# Revit family: Showerhead_Contemporary_Kiwami-Renesse_TS170A_TOTO
name_source: partatom
category: Plumbing Fixtures
revit_build: Autodesk Revit Architecture 2013 (Build: 20130531_2115(x64)
units: mm (PartAtom-declared; Revit-internal decimal feet)

## types (1)
- TS170A
    04 CSI = 22 41 39
    95 CSI = 15416
    Assembly Code = D2010710
    CAD Drawing URL = http://assets.totousa.com
    CW Connection = Yes
    CWFU = 0
    Cold Water Connection Diameter = 1"
    Cold Water Connection Radius = 1/2"
    Cold Water Connector = Cold Water Connection
    Color Availability = #CP Polished Chrome
    Default Elevation = 72"
    Depth = 13"
    Description = Showerhead
    Finish = Metal - TOTO - Chrome - Polished
    Flow Rate = 3.000 GPM
    HW Connection = Yes
    HWFU = 0
    Height = 3 3/4"
    Hot Water Connection Diameter = 1"
    Hot Water Connection Radius = 1/2"
    Hot Water Connector = Hot Water Connection
    Manufacturer = TOTO USA, Inc.
    Manufacturer Fax = (770) 282-0002
    Model = TS170A
    Series = Kiwami Renesse
    Shipping Weight = 4.30 lb
    Spec Sheet URL = http://assets.totousa.com
    Style = Contemporary
    Subcategory = Showers
    Tempered Water Connection NPT = 1"
    Toto BIM Number = BM-00172
    URL = http://www.totousa.com
    Vent Connection = No
    WFU = 0
    Warranty = Lifetime Limited Warranty (Residential Use); One Year Limited (Commercial Use)
    Warranty URL = http://www.totousa.com
    Waste Connection = No
    Width = 2 3/16"

## geometry (parser evidence)
native form markers: Blend x6, Sweep x5
no freeform markers — native parametric forms only
